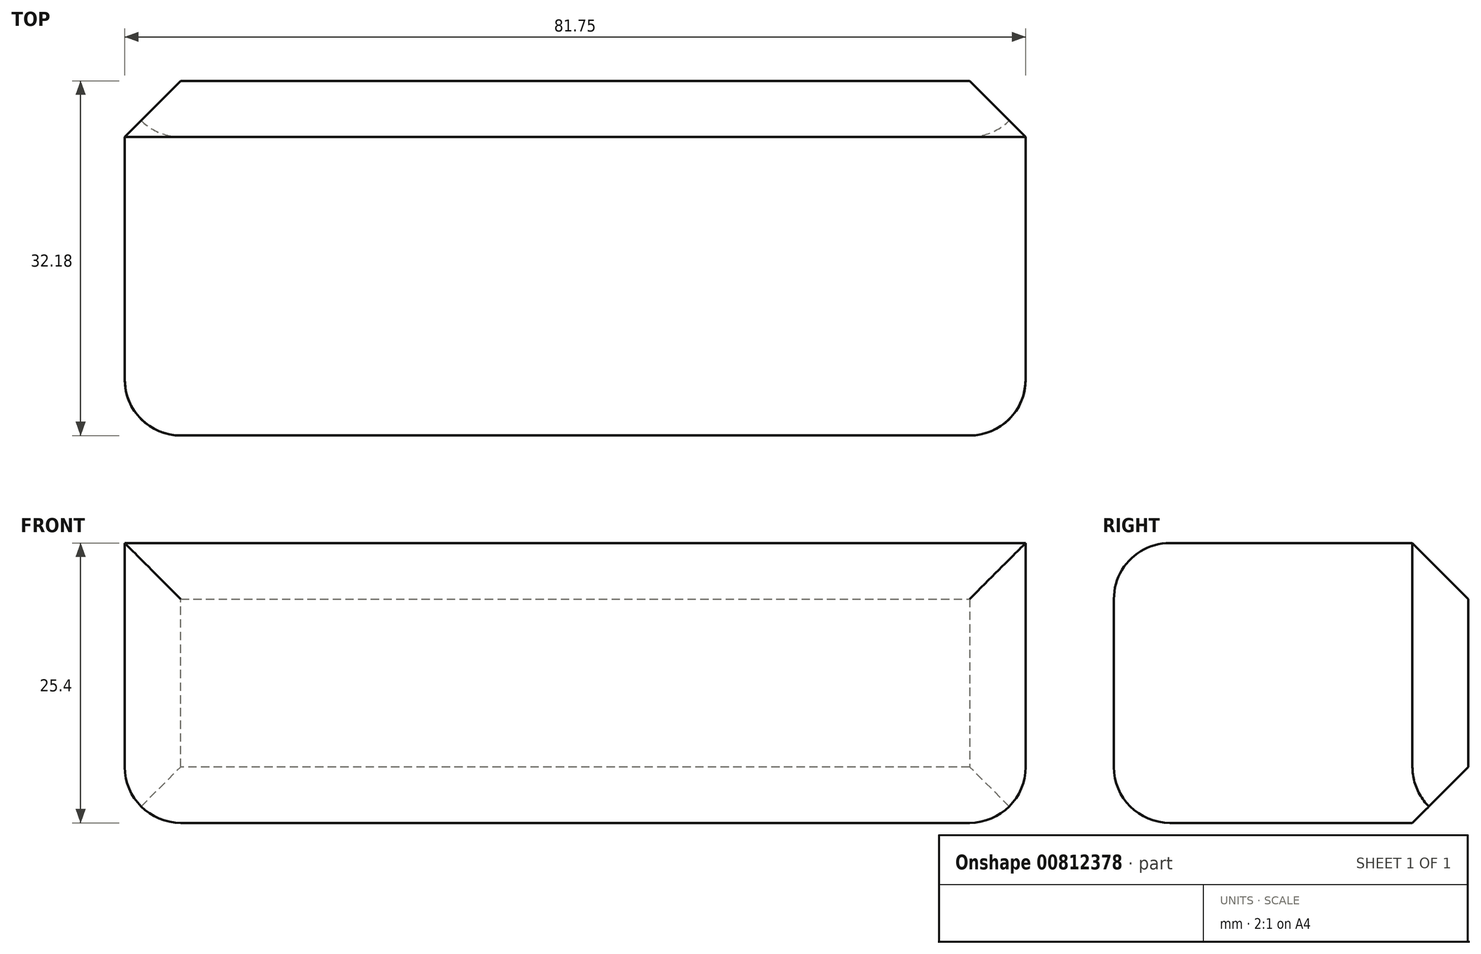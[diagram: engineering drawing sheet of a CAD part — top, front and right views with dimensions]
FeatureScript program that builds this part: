
annotation { "Feature Type Name" : "Feature", "Feature Type Description" : "" }
export const myFeature = defineFeature(function(context is Context, id is Id, definition is map)
    precondition{}
    {
        {
            var Q0;
            Q0=qCreatedBy(makeId("Top.planeOp"),FACE);
            var sketch = newSketch(context, id + "F0", { "sketchPlane" : qUnion([Q0])});
            skLineSegment(sketch, "E0", {"start": v(0, -33.72) * mm, "end": v(-28.55, 0) * mm});
            skLineSegment(sketch, "E1.bottom", {"start": v(19.44, 22.27) * mm, "end": v(-62.31, 22.27) * mm});
            skLineSegment(sketch, "E1.top", {"start": v(19.44, -9.9) * mm, "end": v(-62.31, -9.9) * mm});
            skLineSegment(sketch, "E1.left", {"start": v(19.44, 22.27) * mm, "end": v(19.44, -9.9) * mm});
            skLineSegment(sketch, "E1.right", {"start": v(-62.31, 22.27) * mm, "end": v(-62.31, -9.9) * mm});
            skSolve(sketch);
        }
        {
            var Q0;
            Q0 = qSketchRegion(id + "F0", true);
            extrude(context, id + "F1", {"entities" : qUnion([Q0]), "depth" : 25.4 * mm, "offsetDistance" : 25.4 * mm});
        }
        {
            var Q0;
            Q0=makeQuery(id+"F1.opExtrude","SWEPT_FACE",FACE,{"disambiguationData":[OSD([sQuery(id+"F0.wireOp",EDGE,"E1.bottom")])]});
            chamfer(context, id + "F2", {"entities" : qUnion([Q0]), "width" : 5.08 * mm, "tangentPropagation" : true});
        }
        {
            var Q0;
            Q0=makeQuery(id+"F1.opExtrude","SWEPT_FACE",FACE,{"disambiguationData":[OSD([sQuery(id+"F0.wireOp",EDGE,"E1.top")])]});
            var Q1;
            Q1=makeQuery(id+"F1.opExtrude","CAP_EDGE",EDGE,{"disambiguationData":[OSD([sQuery(id+"F0.wireOp",EDGE,"E1.left")])],"isStart":true});
            var Q2;
            Q2=makeQuery(id+"F1.opExtrude","CAP_EDGE",EDGE,{"disambiguationData":[OSD([sQuery(id+"F0.wireOp",EDGE,"E1.right")])],"isStart":true});
            fillet(context, id + "F3", {"entities" : qUnion([Q0, Q1, Q2]), "radius" : 5.08 * mm, "tangentPropagation" : true, "allowEdgeOverflow" : false});
        }
    });
